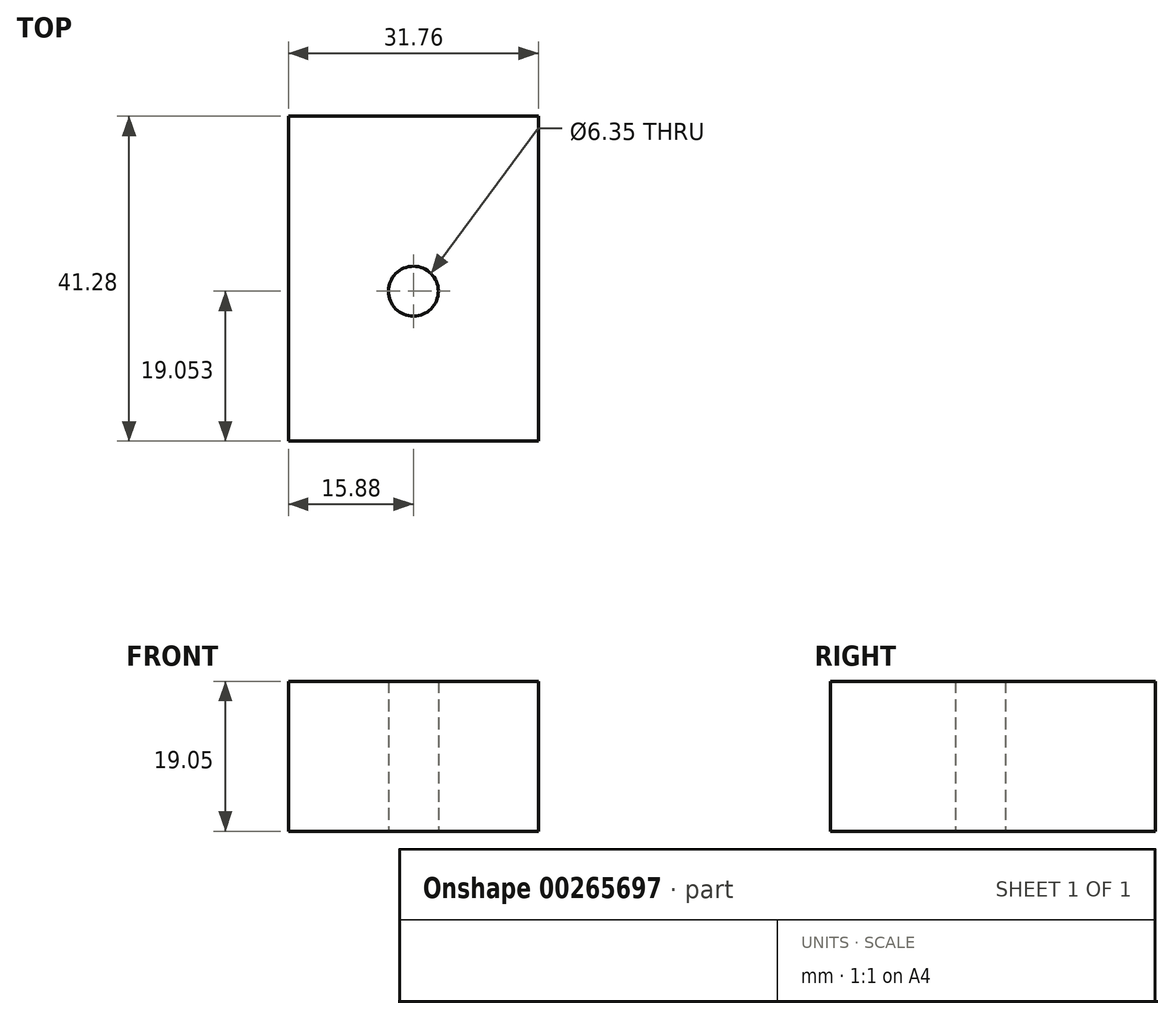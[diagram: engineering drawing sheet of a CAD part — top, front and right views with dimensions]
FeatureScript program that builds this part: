
annotation { "Feature Type Name" : "Feature", "Feature Type Description" : "" }
export const myFeature = defineFeature(function(context is Context, id is Id, definition is map)
    precondition{}
    {
        {
            var Q0;
            Q0=qCreatedBy(makeId("Top.planeOp"),FACE);
            var sketch = newSketch(context, id + "F0", { "sketchPlane" : qUnion([Q0])});
            skLineSegment(sketch, "E0.bottom", {"start": v(15.87, 20.64) * mm, "end": v(-15.88, 20.64) * mm});
            skLineSegment(sketch, "E0.top", {"start": v(15.88, -20.64) * mm, "end": v(-15.87, -20.64) * mm});
            skLineSegment(sketch, "E0.left", {"start": v(15.87, 20.64) * mm, "end": v(15.88, -20.64) * mm});
            skLineSegment(sketch, "E0.right", {"start": v(-15.88, 20.64) * mm, "end": v(-15.87, -20.64) * mm});
            skPoint(sketch, "E0.middle", {"position": v(0, 0) * mm});
            skLineSegment(sketch, "E1", {"start": v(0, 0) * mm, "end": v(0, -20.64) * mm});
            skCircle(sketch, "E2", {"center": v(0, -1.59) * mm, "radius": 3.18 * mm});
            skSolve(sketch);
        }
        {
            var Q0;
            Q0 = qSketchRegion(id + "F0", true);
            extrude(context, id + "F1", {"entities" : qUnion([Q0]), "depth" : 19.05 * mm});
        }
    });
